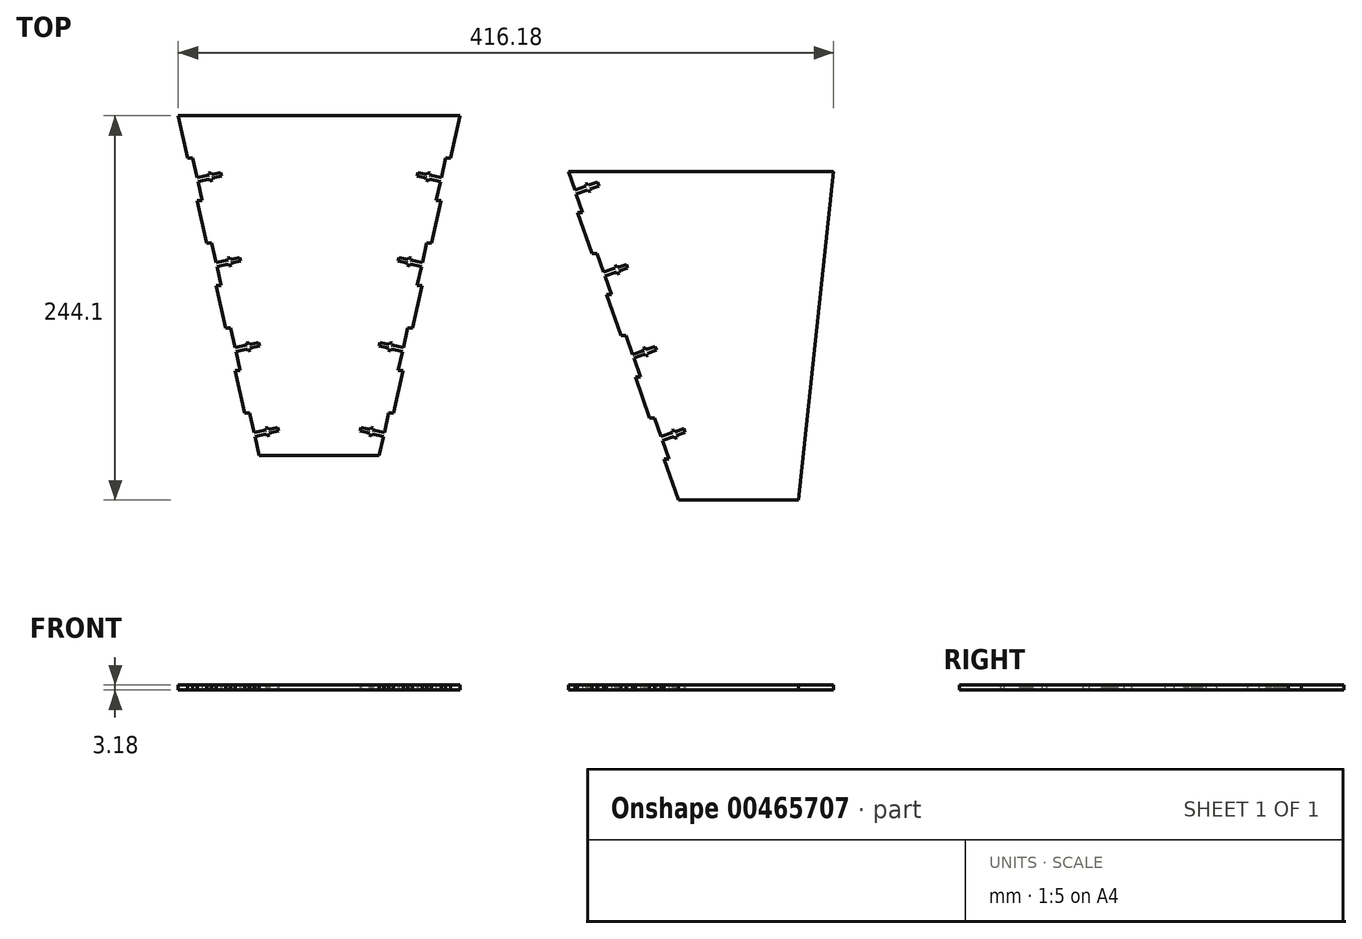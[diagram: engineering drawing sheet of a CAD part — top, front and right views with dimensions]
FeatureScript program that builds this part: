
annotation { "Feature Type Name" : "Feature", "Feature Type Description" : "" }
export const myFeature = defineFeature(function(context is Context, id is Id, definition is map)
    precondition{}
    {
        {
            var Q0;
            Q0=qCreatedBy(makeId("Top.planeOp"),FACE);
            var sketch = newSketch(context, id + "F0", { "sketchPlane" : qUnion([Q0])});
            skLineSegment(sketch, "E0", {"start": v(-1.9, 24.3) * mm, "end": v(74.3, 24.3) * mm});
            skPoint(sketch, "E1", {"position": v(-53.33, 240.2) * mm});
            skPoint(sketch, "E2", {"position": v(125.74, 240.2) * mm});
            skLineSegment(sketch, "E3", {"start": v(-53.33, 240.2) * mm, "end": v(125.74, 240.2) * mm});
            skPoint(sketch, "E4", {"position": v(-29.2, 132.26) * mm});
            skPoint(sketch, "E5", {"position": v(-41.26, 186.23) * mm});
            skPoint(sketch, "E6", {"position": v(-17.13, 78.28) * mm});
            skPoint(sketch, "E7", {"position": v(-47.3, 213.22) * mm});
            skPoint(sketch, "E8", {"position": v(-35.23, 159.25) * mm});
            skPoint(sketch, "E9", {"position": v(-23.17, 105.27) * mm});
            skPoint(sketch, "E10", {"position": v(-11.1, 51.3) * mm});
            skLineSegment(sketch, "E11", {"start": v(-47.3, 213.22) * mm, "end": v(-44.12, 213.22) * mm});
            skLineSegment(sketch, "E12", {"start": v(-41.26, 186.23) * mm, "end": v(-38.09, 186.23) * mm});
            skLineSegment(sketch, "E13", {"start": v(-35.23, 159.25) * mm, "end": v(-32.06, 159.25) * mm});
            skLineSegment(sketch, "E14", {"start": v(-29.2, 132.26) * mm, "end": v(-26.02, 132.26) * mm});
            skLineSegment(sketch, "E15", {"start": v(-23.17, 105.27) * mm, "end": v(-20, 105.27) * mm});
            skLineSegment(sketch, "E16", {"start": v(-17.13, 78.28) * mm, "end": v(-13.96, 78.28) * mm});
            skLineSegment(sketch, "E17", {"start": v(-11.1, 51.3) * mm, "end": v(-7.93, 51.3) * mm});
            skLineSegment(sketch, "E18", {"start": v(-11.1, 51.3) * mm, "end": v(-17.13, 78.28) * mm});
            skLineSegment(sketch, "E19", {"start": v(-23.17, 105.27) * mm, "end": v(-29.2, 132.26) * mm});
            skLineSegment(sketch, "E20", {"start": v(-35.23, 159.25) * mm, "end": v(-41.26, 186.23) * mm});
            skLineSegment(sketch, "E21", {"start": v(-47.3, 213.22) * mm, "end": v(-53.33, 240.2) * mm});
            skPoint(sketch, "E22", {"position": v(36.2, 24.3) * mm});
            skPoint(sketch, "E23", {"position": v(36.2, 240.2) * mm});
            skLineSegment(sketch, "E24", {"start": v(36.2, 240.2) * mm, "end": v(36.2, 24.3) * mm, "construction": true});
            skPoint(sketch, "E25", {"position": v(-33.95, 202.63) * mm});
            skPoint(sketch, "E26", {"position": v(-32.33, 202.99) * mm});
            skLineSegment(sketch, "E27", {"start": v(-33.95, 202.63) * mm, "end": v(-34.22, 203.87) * mm});
            skLineSegment(sketch, "E28", {"start": v(-34.22, 203.87) * mm, "end": v(-32.6, 204.22) * mm});
            skLineSegment(sketch, "E29", {"start": v(-32.6, 204.22) * mm, "end": v(-32.33, 202.99) * mm});
            skLineSegment(sketch, "E30", {"start": v(-26.5, 204.3) * mm, "end": v(-26.23, 203.05) * mm});
            skLineSegment(sketch, "E31", {"start": v(-26.5, 204.3) * mm, "end": v(-32.33, 202.99) * mm});
            skLineSegment(sketch, "E32", {"start": v(-33.95, 202.63) * mm, "end": v(-41.38, 200.97) * mm});
            skLineSegment(sketch, "E33.MirrorCS", {"start": v(-33.4, 200.15) * mm, "end": v(-40.83, 198.49) * mm});
            skLineSegment(sketch, "E34.MirrorCS", {"start": v(-33.4, 200.15) * mm, "end": v(-33.11, 198.91) * mm});
            skLineSegment(sketch, "E35.MirrorCS", {"start": v(-33.11, 198.91) * mm, "end": v(-31.5, 199.27) * mm});
            skLineSegment(sketch, "E36.MirrorCS", {"start": v(-31.5, 199.27) * mm, "end": v(-31.78, 200.5) * mm});
            skLineSegment(sketch, "E37.MirrorCS", {"start": v(-25.95, 201.81) * mm, "end": v(-31.78, 200.5) * mm});
            skLineSegment(sketch, "E38.MirrorCS", {"start": v(-25.95, 201.81) * mm, "end": v(-26.23, 203.05) * mm});
            skLineSegment(sketch, "E39", {"start": v(-44.12, 213.22) * mm, "end": v(-41.38, 200.97) * mm});
            skLineSegment(sketch, "E40", {"start": v(-40.83, 198.49) * mm, "end": v(-38.09, 186.23) * mm});
            skLineSegment(sketch, "E41.1.0.0", {"start": v(-21.88, 148.65) * mm, "end": v(-29.32, 147) * mm});
            skLineSegment(sketch, "E41.1.0.1", {"start": v(-14.44, 150.32) * mm, "end": v(-14.17, 149.08) * mm});
            skLineSegment(sketch, "E41.1.0.2", {"start": v(-20.54, 150.25) * mm, "end": v(-20.27, 149.01) * mm});
            skLineSegment(sketch, "E41.1.0.3", {"start": v(-21.33, 146.17) * mm, "end": v(-21.05, 144.94) * mm});
            skLineSegment(sketch, "E41.1.0.4", {"start": v(-21.33, 146.17) * mm, "end": v(-28.76, 144.51) * mm});
            skLineSegment(sketch, "E41.1.0.5", {"start": v(-21.88, 148.65) * mm, "end": v(-22.15, 149.9) * mm});
            skLineSegment(sketch, "E41.1.0.6", {"start": v(-13.89, 147.84) * mm, "end": v(-14.17, 149.08) * mm});
            skLineSegment(sketch, "E41.1.0.7", {"start": v(-22.15, 149.9) * mm, "end": v(-20.54, 150.25) * mm});
            skLineSegment(sketch, "E41.1.0.8", {"start": v(-13.89, 147.84) * mm, "end": v(-19.72, 146.53) * mm});
            skPoint(sketch, "E41.1.0.9", {"position": v(-21.88, 148.65) * mm});
            skLineSegment(sketch, "E41.1.0.10", {"start": v(-14.44, 150.32) * mm, "end": v(-20.27, 149.01) * mm});
            skLineSegment(sketch, "E41.1.0.11", {"start": v(-19.44, 145.3) * mm, "end": v(-19.72, 146.53) * mm});
            skLineSegment(sketch, "E41.1.0.12", {"start": v(-21.05, 144.94) * mm, "end": v(-19.44, 145.3) * mm});
            skPoint(sketch, "E41.1.0.13", {"position": v(-20.27, 149.01) * mm});
            skLineSegment(sketch, "E41.2.0.0", {"start": v(-9.82, 94.68) * mm, "end": v(-17.25, 93.02) * mm});
            skLineSegment(sketch, "E41.2.0.1", {"start": v(-2.38, 96.34) * mm, "end": v(-2.1, 95.1) * mm});
            skLineSegment(sketch, "E41.2.0.2", {"start": v(-8.48, 96.27) * mm, "end": v(-8.2, 95.04) * mm});
            skLineSegment(sketch, "E41.2.0.3", {"start": v(-9.26, 92.2) * mm, "end": v(-8.98, 90.96) * mm});
            skLineSegment(sketch, "E41.2.0.4", {"start": v(-9.26, 92.2) * mm, "end": v(-16.7, 90.54) * mm});
            skLineSegment(sketch, "E41.2.0.5", {"start": v(-9.82, 94.68) * mm, "end": v(-10.1, 95.92) * mm});
            skLineSegment(sketch, "E41.2.0.6", {"start": v(-1.83, 93.86) * mm, "end": v(-2.1, 95.1) * mm});
            skLineSegment(sketch, "E41.2.0.7", {"start": v(-10.1, 95.92) * mm, "end": v(-8.48, 96.27) * mm});
            skLineSegment(sketch, "E41.2.0.8", {"start": v(-1.83, 93.86) * mm, "end": v(-7.65, 92.56) * mm});
            skPoint(sketch, "E41.2.0.9", {"position": v(-9.82, 94.68) * mm});
            skLineSegment(sketch, "E41.2.0.10", {"start": v(-2.38, 96.34) * mm, "end": v(-8.2, 95.04) * mm});
            skLineSegment(sketch, "E41.2.0.11", {"start": v(-7.37, 91.32) * mm, "end": v(-7.65, 92.56) * mm});
            skLineSegment(sketch, "E41.2.0.12", {"start": v(-8.98, 90.96) * mm, "end": v(-7.37, 91.32) * mm});
            skPoint(sketch, "E41.2.0.13", {"position": v(-8.2, 95.04) * mm});
            skLineSegment(sketch, "E41.3.0.0", {"start": v(2.25, 40.7) * mm, "end": v(-5.19, 39.04) * mm});
            skLineSegment(sketch, "E41.3.0.1", {"start": v(9.69, 42.37) * mm, "end": v(9.96, 41.13) * mm});
            skLineSegment(sketch, "E41.3.0.2", {"start": v(3.59, 42.3) * mm, "end": v(3.86, 41.06) * mm});
            skLineSegment(sketch, "E41.3.0.3", {"start": v(2.8, 38.22) * mm, "end": v(3.08, 36.99) * mm});
            skLineSegment(sketch, "E41.3.0.4", {"start": v(2.8, 38.22) * mm, "end": v(-4.63, 36.56) * mm});
            skLineSegment(sketch, "E41.3.0.5", {"start": v(2.25, 40.7) * mm, "end": v(1.97, 41.94) * mm});
            skLineSegment(sketch, "E41.3.0.6", {"start": v(10.24, 39.89) * mm, "end": v(9.96, 41.13) * mm});
            skLineSegment(sketch, "E41.3.0.7", {"start": v(1.97, 41.94) * mm, "end": v(3.59, 42.3) * mm});
            skLineSegment(sketch, "E41.3.0.8", {"start": v(10.24, 39.89) * mm, "end": v(4.41, 38.58) * mm});
            skPoint(sketch, "E41.3.0.9", {"position": v(2.25, 40.7) * mm});
            skLineSegment(sketch, "E41.3.0.10", {"start": v(9.69, 42.37) * mm, "end": v(3.86, 41.06) * mm});
            skLineSegment(sketch, "E41.3.0.11", {"start": v(4.7, 37.35) * mm, "end": v(4.41, 38.58) * mm});
            skLineSegment(sketch, "E41.3.0.12", {"start": v(3.08, 36.99) * mm, "end": v(4.7, 37.35) * mm});
            skPoint(sketch, "E41.3.0.13", {"position": v(3.86, 41.06) * mm});
            skLineSegment(sketch, "E42", {"start": v(-7.93, 51.3) * mm, "end": v(-5.19, 39.04) * mm});
            skLineSegment(sketch, "E43", {"start": v(-4.63, 36.56) * mm, "end": v(-1.9, 24.3) * mm});
            skLineSegment(sketch, "E44", {"start": v(-32.06, 159.25) * mm, "end": v(-29.32, 147) * mm});
            skLineSegment(sketch, "E45", {"start": v(-28.76, 144.51) * mm, "end": v(-26.02, 132.26) * mm});
            skLineSegment(sketch, "E46", {"start": v(-20, 105.27) * mm, "end": v(-17.25, 93.02) * mm});
            skLineSegment(sketch, "E47", {"start": v(-16.7, 90.54) * mm, "end": v(-13.96, 78.28) * mm});
            skLineSegment(sketch, "E48.MirrorCS", {"start": v(105.8, 200.15) * mm, "end": v(105.52, 198.91) * mm});
            skLineSegment(sketch, "E49.MirrorCS", {"start": v(105.02, 204.22) * mm, "end": v(104.75, 202.99) * mm});
            skLineSegment(sketch, "E50.MirrorCS", {"start": v(103.91, 199.27) * mm, "end": v(104.2, 200.5) * mm});
            skLineSegment(sketch, "E51.MirrorCS", {"start": v(69.33, 36.99) * mm, "end": v(67.72, 37.35) * mm});
            skLineSegment(sketch, "E52.MirrorCS", {"start": v(68.83, 42.3) * mm, "end": v(68.55, 41.06) * mm});
            skLineSegment(sketch, "E53.MirrorCS", {"start": v(98.92, 204.3) * mm, "end": v(104.75, 202.99) * mm});
            skLineSegment(sketch, "E54.MirrorCS", {"start": v(106.36, 202.63) * mm, "end": v(106.63, 203.87) * mm});
            skLineSegment(sketch, "E55.MirrorCS", {"start": v(98.37, 201.81) * mm, "end": v(98.64, 203.05) * mm});
            skLineSegment(sketch, "E56.MirrorCS", {"start": v(70.16, 40.7) * mm, "end": v(70.44, 41.94) * mm});
            skLineSegment(sketch, "E57.MirrorCS", {"start": v(67.72, 37.35) * mm, "end": v(68, 38.58) * mm});
            skLineSegment(sketch, "E58.MirrorCS", {"start": v(70.44, 41.94) * mm, "end": v(68.83, 42.3) * mm});
            skLineSegment(sketch, "E59.MirrorCS", {"start": v(106.63, 203.87) * mm, "end": v(105.02, 204.22) * mm});
            skLineSegment(sketch, "E60.MirrorCS", {"start": v(105.52, 198.91) * mm, "end": v(103.91, 199.27) * mm});
            skLineSegment(sketch, "E61.MirrorCS", {"start": v(69.6, 38.22) * mm, "end": v(69.33, 36.99) * mm});
            skLineSegment(sketch, "E62.MirrorCS", {"start": v(92.95, 150.25) * mm, "end": v(92.68, 149.01) * mm});
            skLineSegment(sketch, "E63.MirrorCS", {"start": v(82.5, 95.92) * mm, "end": v(80.9, 96.27) * mm});
            skLineSegment(sketch, "E64.MirrorCS", {"start": v(93.74, 146.17) * mm, "end": v(93.46, 144.94) * mm});
            skLineSegment(sketch, "E65.MirrorCS", {"start": v(80.9, 96.27) * mm, "end": v(80.62, 95.04) * mm});
            skLineSegment(sketch, "E66.MirrorCS", {"start": v(98.37, 201.81) * mm, "end": v(104.2, 200.5) * mm});
            skLineSegment(sketch, "E67.MirrorCS", {"start": v(98.92, 204.3) * mm, "end": v(98.64, 203.05) * mm});
            skLineSegment(sketch, "E68.MirrorCS", {"start": v(91.85, 145.3) * mm, "end": v(92.13, 146.53) * mm});
            skLineSegment(sketch, "E69.MirrorCS", {"start": v(94.3, 148.65) * mm, "end": v(94.57, 149.9) * mm});
            skLineSegment(sketch, "E70.MirrorCS", {"start": v(79.78, 91.32) * mm, "end": v(80.06, 92.56) * mm});
            skLineSegment(sketch, "E71.MirrorCS", {"start": v(82.23, 94.68) * mm, "end": v(82.5, 95.92) * mm});
            skLineSegment(sketch, "E72.MirrorCS", {"start": v(94.57, 149.9) * mm, "end": v(92.95, 150.25) * mm});
            skLineSegment(sketch, "E73.MirrorCS", {"start": v(93.46, 144.94) * mm, "end": v(91.85, 145.3) * mm});
            skLineSegment(sketch, "E74.MirrorCS", {"start": v(83.51, 51.3) * mm, "end": v(80.34, 51.3) * mm});
            skLineSegment(sketch, "E75.MirrorCS", {"start": v(89.55, 78.28) * mm, "end": v(86.37, 78.28) * mm});
            skLineSegment(sketch, "E76.MirrorCS", {"start": v(95.58, 105.27) * mm, "end": v(92.4, 105.27) * mm});
            skLineSegment(sketch, "E77.MirrorCS", {"start": v(101.61, 132.26) * mm, "end": v(98.44, 132.26) * mm});
            skLineSegment(sketch, "E78.MirrorCS", {"start": v(119.7, 213.22) * mm, "end": v(116.53, 213.22) * mm});
            skLineSegment(sketch, "E79.MirrorCS", {"start": v(113.68, 186.23) * mm, "end": v(110.5, 186.23) * mm});
            skLineSegment(sketch, "E80.MirrorCS", {"start": v(107.64, 159.25) * mm, "end": v(104.47, 159.25) * mm});
            skLineSegment(sketch, "E81.MirrorCS", {"start": v(62.73, 42.37) * mm, "end": v(68.55, 41.06) * mm});
            skLineSegment(sketch, "E82.MirrorCS", {"start": v(81.4, 90.96) * mm, "end": v(79.78, 91.32) * mm});
            skLineSegment(sketch, "E83.MirrorCS", {"start": v(81.67, 92.2) * mm, "end": v(81.4, 90.96) * mm});
            skLineSegment(sketch, "E84.MirrorCS", {"start": v(86.3, 147.84) * mm, "end": v(86.58, 149.08) * mm});
            skLineSegment(sketch, "E85.MirrorCS", {"start": v(86.86, 150.32) * mm, "end": v(92.68, 149.01) * mm});
            skLineSegment(sketch, "E86.MirrorCS", {"start": v(74.24, 93.86) * mm, "end": v(74.51, 95.1) * mm});
            skLineSegment(sketch, "E87.MirrorCS", {"start": v(93.74, 146.17) * mm, "end": v(101.17, 144.51) * mm});
            skLineSegment(sketch, "E88.MirrorCS", {"start": v(74.24, 93.86) * mm, "end": v(80.06, 92.56) * mm});
            skLineSegment(sketch, "E89.MirrorCS", {"start": v(105.8, 200.15) * mm, "end": v(113.24, 198.49) * mm});
            skLineSegment(sketch, "E90.MirrorCS", {"start": v(62.17, 39.89) * mm, "end": v(68, 38.58) * mm});
            skLineSegment(sketch, "E91.MirrorCS", {"start": v(62.73, 42.37) * mm, "end": v(62.45, 41.13) * mm});
            skLineSegment(sketch, "E92.MirrorCS", {"start": v(69.6, 38.22) * mm, "end": v(77.05, 36.56) * mm});
            skLineSegment(sketch, "E93.MirrorCS", {"start": v(82.23, 94.68) * mm, "end": v(89.66, 93.02) * mm});
            skLineSegment(sketch, "E94.MirrorCS", {"start": v(70.16, 40.7) * mm, "end": v(77.6, 39.04) * mm});
            skLineSegment(sketch, "E95.MirrorCS", {"start": v(106.36, 202.63) * mm, "end": v(113.8, 200.97) * mm});
            skLineSegment(sketch, "E96.MirrorCS", {"start": v(74.8, 96.34) * mm, "end": v(74.51, 95.1) * mm});
            skLineSegment(sketch, "E97.MirrorCS", {"start": v(94.3, 148.65) * mm, "end": v(101.73, 147) * mm});
            skLineSegment(sketch, "E98.MirrorCS", {"start": v(74.8, 96.34) * mm, "end": v(80.62, 95.04) * mm});
            skLineSegment(sketch, "E99.MirrorCS", {"start": v(81.67, 92.2) * mm, "end": v(89.11, 90.54) * mm});
            skLineSegment(sketch, "E100.MirrorCS", {"start": v(86.86, 150.32) * mm, "end": v(86.58, 149.08) * mm});
            skLineSegment(sketch, "E101.MirrorCS", {"start": v(62.17, 39.89) * mm, "end": v(62.45, 41.13) * mm});
            skLineSegment(sketch, "E102.MirrorCS", {"start": v(86.3, 147.84) * mm, "end": v(92.13, 146.53) * mm});
            skLineSegment(sketch, "E103.MirrorCS", {"start": v(116.53, 213.22) * mm, "end": v(113.8, 200.97) * mm});
            skPoint(sketch, "E104.MirrorP", {"position": v(104.75, 202.99) * mm});
            skLineSegment(sketch, "E105.MirrorCS", {"start": v(77.05, 36.56) * mm, "end": v(74.3, 24.3) * mm});
            skLineSegment(sketch, "E106.MirrorCS", {"start": v(119.7, 213.22) * mm, "end": v(125.74, 240.2) * mm});
            skPoint(sketch, "E107.MirrorP", {"position": v(89.55, 78.28) * mm});
            skLineSegment(sketch, "E108.MirrorCS", {"start": v(89.11, 90.54) * mm, "end": v(86.37, 78.28) * mm});
            skLineSegment(sketch, "E109.MirrorCS", {"start": v(80.34, 51.3) * mm, "end": v(77.6, 39.04) * mm});
            skPoint(sketch, "E110.MirrorP", {"position": v(113.68, 186.23) * mm});
            skPoint(sketch, "E111.MirrorP", {"position": v(101.61, 132.26) * mm});
            skPoint(sketch, "E112.MirrorP", {"position": v(68.55, 41.06) * mm});
            skPoint(sketch, "E113.MirrorP", {"position": v(106.36, 202.63) * mm});
            skLineSegment(sketch, "E114.MirrorCS", {"start": v(107.64, 159.25) * mm, "end": v(113.68, 186.23) * mm});
            skLineSegment(sketch, "E115.MirrorCS", {"start": v(95.58, 105.27) * mm, "end": v(101.61, 132.26) * mm});
            skLineSegment(sketch, "E116.MirrorCS", {"start": v(83.51, 51.3) * mm, "end": v(89.55, 78.28) * mm});
            skLineSegment(sketch, "E117.MirrorCS", {"start": v(113.24, 198.49) * mm, "end": v(110.5, 186.23) * mm});
            skPoint(sketch, "E118.MirrorP", {"position": v(80.62, 95.04) * mm});
            skPoint(sketch, "E119.MirrorP", {"position": v(82.23, 94.68) * mm});
            skLineSegment(sketch, "E120.MirrorCS", {"start": v(101.17, 144.51) * mm, "end": v(98.44, 132.26) * mm});
            skPoint(sketch, "E121.MirrorP", {"position": v(107.64, 159.25) * mm});
            skPoint(sketch, "E122.MirrorP", {"position": v(94.3, 148.65) * mm});
            skPoint(sketch, "E123.MirrorP", {"position": v(95.58, 105.27) * mm});
            skLineSegment(sketch, "E124.MirrorCS", {"start": v(92.4, 105.27) * mm, "end": v(89.66, 93.02) * mm});
            skLineSegment(sketch, "E125.MirrorCS", {"start": v(104.47, 159.25) * mm, "end": v(101.73, 147) * mm});
            skPoint(sketch, "E126.MirrorP", {"position": v(83.51, 51.3) * mm});
            skPoint(sketch, "E127.MirrorP", {"position": v(119.7, 213.22) * mm});
            skPoint(sketch, "E128.MirrorP", {"position": v(92.68, 149.01) * mm});
            skPoint(sketch, "E129.MirrorP", {"position": v(70.16, 40.7) * mm});
            skPoint(sketch, "E130", {"position": v(122.57, 240.2) * mm});
            skLineSegment(sketch, "E131", {"start": v(264.34, -3.9) * mm, "end": v(340.54, -3.9) * mm});
            skLineSegment(sketch, "E132", {"start": v(340.54, -3.9) * mm, "end": v(362.85, 204.9) * mm});
            skPoint(sketch, "E133", {"position": v(191.22, 204.9) * mm});
            skPoint(sketch, "E134", {"position": v(362.85, 204.9) * mm});
            skPoint(sketch, "E135", {"position": v(264.34, -3.9) * mm});
            skPoint(sketch, "E136", {"position": v(340.54, -3.9) * mm});
            skLineSegment(sketch, "E137", {"start": v(194.4, 204.9) * mm, "end": v(362.85, 204.9) * mm});
            skPoint(sketch, "E138", {"position": v(194.4, 204.9) * mm});
            skPoint(sketch, "E139", {"position": v(227.78, 100.5) * mm});
            skPoint(sketch, "E140", {"position": v(209.5, 152.7) * mm});
            skPoint(sketch, "E141", {"position": v(246.06, 48.3) * mm});
            skPoint(sketch, "E142", {"position": v(200.36, 178.8) * mm});
            skPoint(sketch, "E143", {"position": v(218.64, 126.6) * mm});
            skPoint(sketch, "E144", {"position": v(236.92, 74.4) * mm});
            skPoint(sketch, "E145", {"position": v(255.2, 22.2) * mm});
            skLineSegment(sketch, "E146", {"start": v(200.36, 178.8) * mm, "end": v(203.53, 178.8) * mm});
            skLineSegment(sketch, "E147", {"start": v(209.5, 152.7) * mm, "end": v(212.67, 152.7) * mm});
            skLineSegment(sketch, "E148", {"start": v(218.64, 126.6) * mm, "end": v(221.81, 126.6) * mm});
            skLineSegment(sketch, "E149", {"start": v(227.78, 100.5) * mm, "end": v(230.95, 100.5) * mm});
            skLineSegment(sketch, "E150", {"start": v(236.92, 74.4) * mm, "end": v(240.1, 74.4) * mm});
            skLineSegment(sketch, "E151", {"start": v(246.06, 48.3) * mm, "end": v(249.23, 48.3) * mm});
            skLineSegment(sketch, "E152", {"start": v(255.2, 22.2) * mm, "end": v(258.37, 22.2) * mm});
            skLineSegment(sketch, "E153", {"start": v(264.34, -3.9) * mm, "end": v(255.2, 22.2) * mm});
            skLineSegment(sketch, "E154", {"start": v(246.06, 48.3) * mm, "end": v(236.92, 74.4) * mm});
            skLineSegment(sketch, "E155", {"start": v(227.78, 100.5) * mm, "end": v(218.64, 126.6) * mm});
            skLineSegment(sketch, "E156", {"start": v(221.81, 126.6) * mm, "end": v(217.66, 138.46) * mm});
            skLineSegment(sketch, "E157", {"start": v(209.5, 152.7) * mm, "end": v(200.36, 178.8) * mm});
            skLineSegment(sketch, "E158", {"start": v(203.53, 178.8) * mm, "end": v(199.38, 190.66) * mm});
            skPoint(sketch, "E159", {"position": v(198.54, 193.05) * mm});
            skPoint(sketch, "E160", {"position": v(205.73, 195.57) * mm});
            skPoint(sketch, "E161", {"position": v(207.3, 196.12) * mm});
            skLineSegment(sketch, "E162", {"start": v(205.73, 195.57) * mm, "end": v(205.31, 196.77) * mm});
            skLineSegment(sketch, "E163", {"start": v(207.3, 196.12) * mm, "end": v(206.87, 197.32) * mm});
            skLineSegment(sketch, "E164", {"start": v(205.31, 196.77) * mm, "end": v(206.87, 197.32) * mm});
            skLineSegment(sketch, "E165", {"start": v(212.93, 198.1) * mm, "end": v(213.35, 196.9) * mm});
            skLineSegment(sketch, "E166", {"start": v(198.54, 193.05) * mm, "end": v(205.73, 195.57) * mm});
            skLineSegment(sketch, "E167", {"start": v(207.3, 196.12) * mm, "end": v(212.93, 198.1) * mm});
            skLineSegment(sketch, "E168.MirrorCS", {"start": v(208.13, 193.72) * mm, "end": v(213.77, 195.7) * mm});
            skLineSegment(sketch, "E169.MirrorCS", {"start": v(213.77, 195.7) * mm, "end": v(213.35, 196.9) * mm});
            skLineSegment(sketch, "E170.MirrorCS", {"start": v(207, 191.98) * mm, "end": v(208.55, 192.52) * mm});
            skLineSegment(sketch, "E171.MirrorCS", {"start": v(208.13, 193.72) * mm, "end": v(208.55, 192.52) * mm});
            skLineSegment(sketch, "E172.MirrorCS", {"start": v(206.57, 193.18) * mm, "end": v(207, 191.98) * mm});
            skLineSegment(sketch, "E173.MirrorCS", {"start": v(199.38, 190.66) * mm, "end": v(206.57, 193.18) * mm});
            skLineSegment(sketch, "E174.1.0.0", {"start": v(225.27, 139.78) * mm, "end": v(226.83, 140.32) * mm});
            skPoint(sketch, "E174.1.0.1", {"position": v(224.01, 143.37) * mm});
            skLineSegment(sketch, "E174.1.0.2", {"start": v(225.57, 143.92) * mm, "end": v(231.2, 145.9) * mm});
            skLineSegment(sketch, "E174.1.0.3", {"start": v(217.66, 138.46) * mm, "end": v(224.85, 140.98) * mm});
            skPoint(sketch, "E174.1.0.4", {"position": v(225.57, 143.92) * mm});
            skLineSegment(sketch, "E174.1.0.5", {"start": v(226.41, 141.52) * mm, "end": v(232.05, 143.5) * mm});
            skPoint(sketch, "E174.1.0.6", {"position": v(216.82, 140.86) * mm});
            skLineSegment(sketch, "E174.1.0.7", {"start": v(216.82, 140.86) * mm, "end": v(224.01, 143.37) * mm});
            skLineSegment(sketch, "E174.1.0.8", {"start": v(225.57, 143.92) * mm, "end": v(225.15, 145.12) * mm});
            skLineSegment(sketch, "E174.1.0.9", {"start": v(226.41, 141.52) * mm, "end": v(226.83, 140.32) * mm});
            skLineSegment(sketch, "E174.1.0.10", {"start": v(223.6, 144.57) * mm, "end": v(225.15, 145.12) * mm});
            skLineSegment(sketch, "E174.1.0.11", {"start": v(224.85, 140.98) * mm, "end": v(225.27, 139.78) * mm});
            skLineSegment(sketch, "E174.1.0.12", {"start": v(231.2, 145.9) * mm, "end": v(231.63, 144.7) * mm});
            skLineSegment(sketch, "E174.1.0.13", {"start": v(232.05, 143.5) * mm, "end": v(231.63, 144.7) * mm});
            skLineSegment(sketch, "E174.1.0.14", {"start": v(224.01, 143.37) * mm, "end": v(223.6, 144.57) * mm});
            skLineSegment(sketch, "E174.2.0.0", {"start": v(243.55, 87.58) * mm, "end": v(245.11, 88.12) * mm});
            skPoint(sketch, "E174.2.0.1", {"position": v(242.3, 91.17) * mm});
            skLineSegment(sketch, "E174.2.0.2", {"start": v(243.85, 91.72) * mm, "end": v(249.49, 93.7) * mm});
            skLineSegment(sketch, "E174.2.0.3", {"start": v(235.94, 86.26) * mm, "end": v(243.13, 88.78) * mm});
            skPoint(sketch, "E174.2.0.4", {"position": v(243.85, 91.72) * mm});
            skLineSegment(sketch, "E174.2.0.5", {"start": v(244.7, 89.32) * mm, "end": v(250.33, 91.3) * mm});
            skPoint(sketch, "E174.2.0.6", {"position": v(235.1, 88.66) * mm});
            skLineSegment(sketch, "E174.2.0.7", {"start": v(235.1, 88.66) * mm, "end": v(242.3, 91.17) * mm});
            skLineSegment(sketch, "E174.2.0.8", {"start": v(243.85, 91.72) * mm, "end": v(243.43, 92.92) * mm});
            skLineSegment(sketch, "E174.2.0.9", {"start": v(244.7, 89.32) * mm, "end": v(245.11, 88.12) * mm});
            skLineSegment(sketch, "E174.2.0.10", {"start": v(241.87, 92.37) * mm, "end": v(243.43, 92.92) * mm});
            skLineSegment(sketch, "E174.2.0.11", {"start": v(243.13, 88.78) * mm, "end": v(243.55, 87.58) * mm});
            skLineSegment(sketch, "E174.2.0.12", {"start": v(249.49, 93.7) * mm, "end": v(249.9, 92.5) * mm});
            skLineSegment(sketch, "E174.2.0.13", {"start": v(250.33, 91.3) * mm, "end": v(249.9, 92.5) * mm});
            skLineSegment(sketch, "E174.2.0.14", {"start": v(242.3, 91.17) * mm, "end": v(241.87, 92.37) * mm});
            skLineSegment(sketch, "E174.3.0.0", {"start": v(261.83, 35.38) * mm, "end": v(263.4, 35.93) * mm});
            skPoint(sketch, "E174.3.0.1", {"position": v(260.57, 38.98) * mm});
            skLineSegment(sketch, "E174.3.0.2", {"start": v(262.13, 39.52) * mm, "end": v(267.77, 41.5) * mm});
            skLineSegment(sketch, "E174.3.0.3", {"start": v(254.22, 34.06) * mm, "end": v(261.41, 36.58) * mm});
            skPoint(sketch, "E174.3.0.4", {"position": v(262.13, 39.52) * mm});
            skLineSegment(sketch, "E174.3.0.5", {"start": v(262.97, 37.12) * mm, "end": v(268.6, 39.1) * mm});
            skPoint(sketch, "E174.3.0.6", {"position": v(253.38, 36.46) * mm});
            skLineSegment(sketch, "E174.3.0.7", {"start": v(253.38, 36.46) * mm, "end": v(260.57, 38.98) * mm});
            skLineSegment(sketch, "E174.3.0.8", {"start": v(262.13, 39.52) * mm, "end": v(261.71, 40.72) * mm});
            skLineSegment(sketch, "E174.3.0.9", {"start": v(262.97, 37.12) * mm, "end": v(263.4, 35.93) * mm});
            skLineSegment(sketch, "E174.3.0.10", {"start": v(260.15, 40.17) * mm, "end": v(261.71, 40.72) * mm});
            skLineSegment(sketch, "E174.3.0.11", {"start": v(261.41, 36.58) * mm, "end": v(261.83, 35.38) * mm});
            skLineSegment(sketch, "E174.3.0.12", {"start": v(267.77, 41.5) * mm, "end": v(268.19, 40.3) * mm});
            skLineSegment(sketch, "E174.3.0.13", {"start": v(268.6, 39.1) * mm, "end": v(268.19, 40.3) * mm});
            skLineSegment(sketch, "E174.3.0.14", {"start": v(260.57, 38.98) * mm, "end": v(260.15, 40.17) * mm});
            skLineSegment(sketch, "E175", {"start": v(249.23, 48.3) * mm, "end": v(253.38, 36.46) * mm});
            skLineSegment(sketch, "E176", {"start": v(254.22, 34.06) * mm, "end": v(258.37, 22.2) * mm});
            skLineSegment(sketch, "E177", {"start": v(230.95, 100.5) * mm, "end": v(235.1, 88.66) * mm});
            skLineSegment(sketch, "E178", {"start": v(235.94, 86.26) * mm, "end": v(240.1, 74.4) * mm});
            skLineSegment(sketch, "E179.trimOffspring", {"start": v(216.82, 140.86) * mm, "end": v(212.67, 152.7) * mm});
            skLineSegment(sketch, "E180.trimOffspring", {"start": v(198.54, 193.05) * mm, "end": v(194.4, 204.9) * mm});
            skSolve(sketch);
        }
        {
            var Q0;
            Q0=makeQuery(id+"F0.imprint","IMPRINT",FACE,{"disambiguationData":[TD([[makeQuery(id+"F0.imprint","IMPRINT",EDGE,{"derivedFrom":sQuery(id+"F0.wireOp",EDGE,"E0")}),1.0]])]});
            var Q1;
            Q1=makeQuery(id+"F0.imprint","IMPRINT",FACE,{"disambiguationData":[TD([[makeQuery(id+"F0.imprint","IMPRINT",EDGE,{"derivedFrom":sQuery(id+"F0.wireOp",EDGE,"E131")}),1.0]])]});
            extrude(context, id + "F1", {"entities" : qUnion([Q0, Q1]), "depth" : 3.17 * mm});
        }
    });
